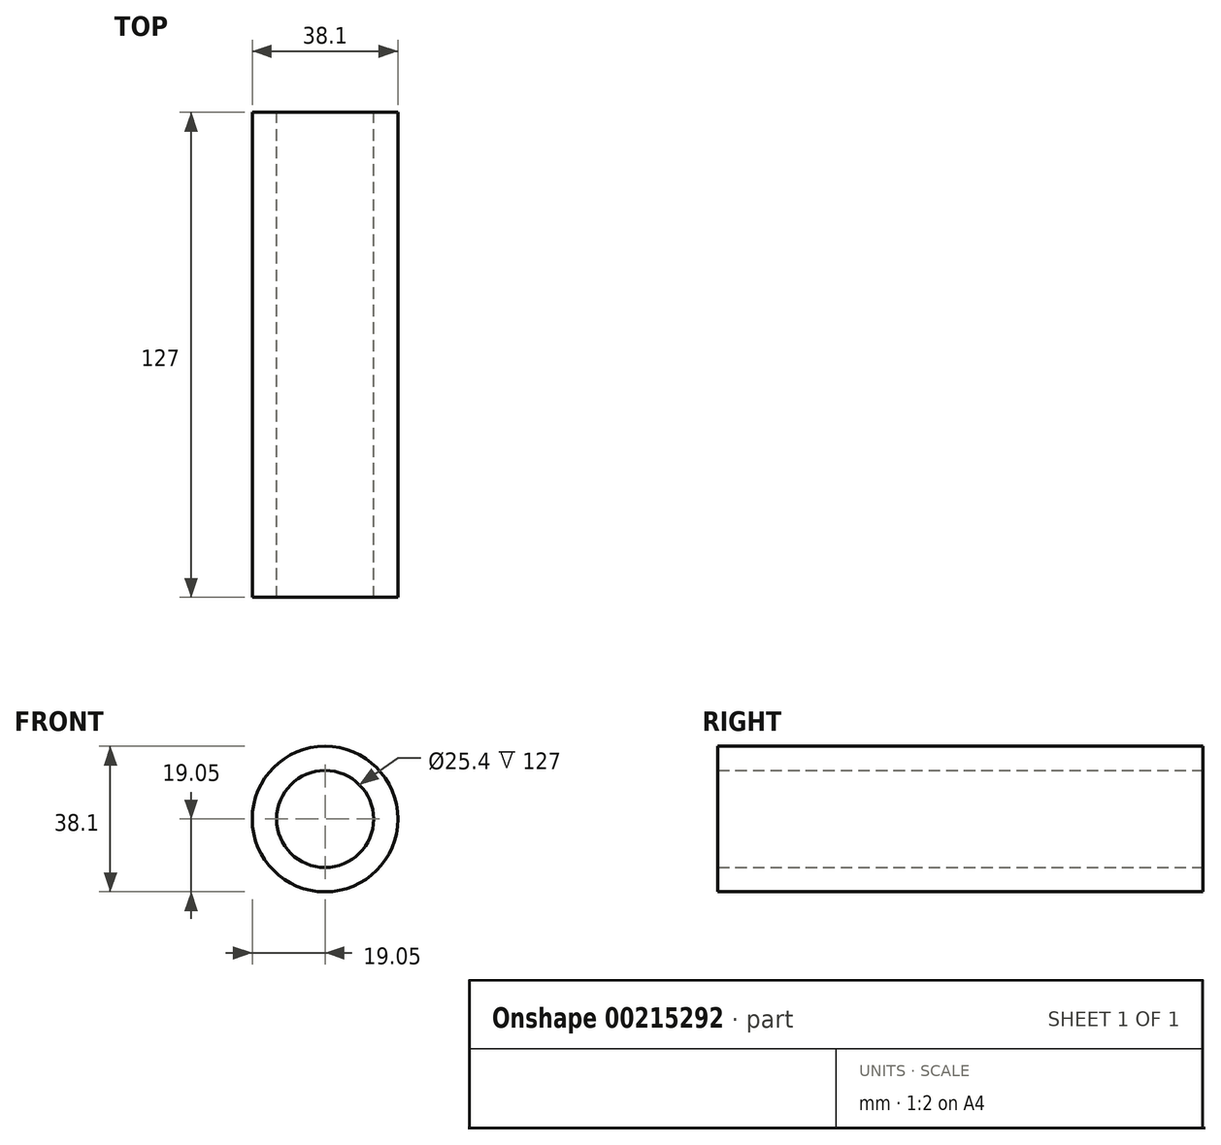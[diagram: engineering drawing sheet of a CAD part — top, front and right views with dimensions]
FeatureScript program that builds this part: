
annotation { "Feature Type Name" : "Feature", "Feature Type Description" : "" }
export const myFeature = defineFeature(function(context is Context, id is Id, definition is map)
    precondition{}
    {
        {
            var Q0;
            Q0=qCreatedBy(makeId("Front.planeOp"),FACE);
            var sketch = newSketch(context, id + "F0", { "sketchPlane" : qUnion([Q0])});
            skCircle(sketch, "E0", {"center": v(0, 0) * mm, "radius": 19.05 * mm});
            skCircle(sketch, "E1", {"center": v(0, 0) * mm, "radius": 12.7 * mm});
            skSolve(sketch);
        }
        {
            var Q0;
            Q0 = qSketchRegion(id + "F0", true);
            var Q1;
            Q1=makeQuery(id+"F0.imprint","IMPRINT",FACE,{"disambiguationData":[TD([[makeQuery(id+"F0.imprint","IMPRINT",EDGE,{"derivedFrom":sQuery(id+"F0.wireOp",EDGE,"E0")}),1.0]])]});
            extrude(context, id + "F1", {"entities" : qUnion([Q0, Q1]), "endBound" : BoundingType.SYMMETRIC, "depth" : 127 * mm});
        }
    });
